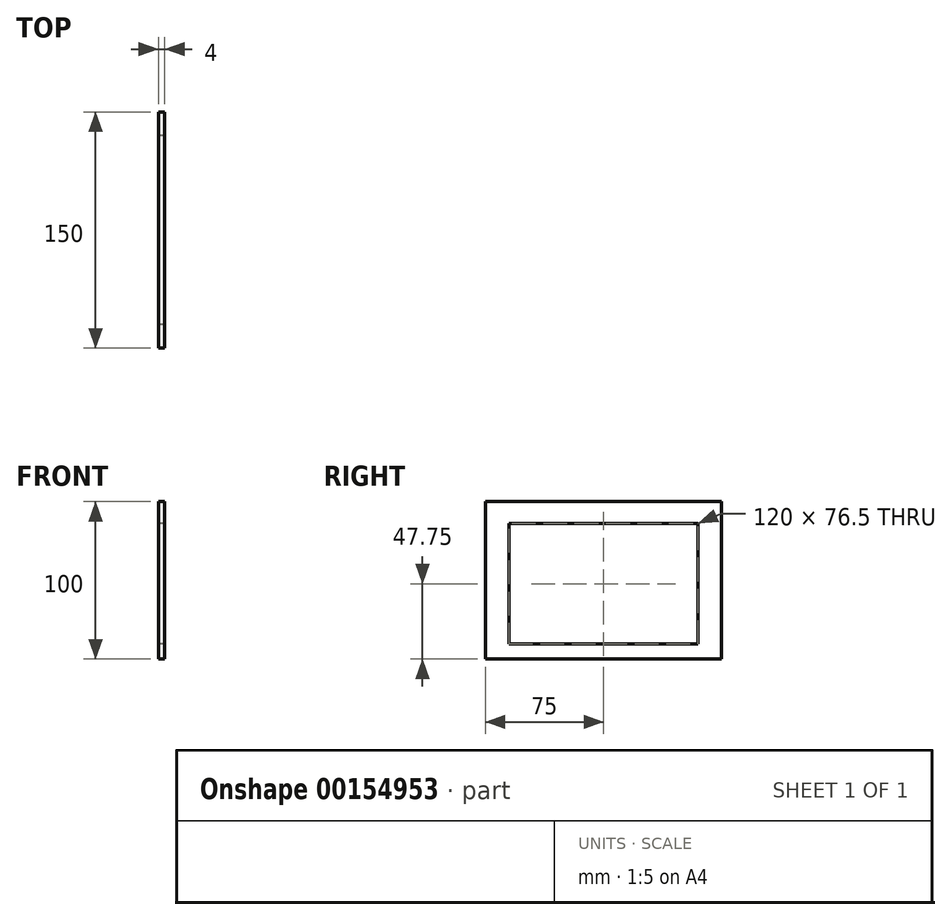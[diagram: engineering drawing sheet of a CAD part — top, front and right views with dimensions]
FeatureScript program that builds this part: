
annotation { "Feature Type Name" : "Feature", "Feature Type Description" : "" }
export const myFeature = defineFeature(function(context is Context, id is Id, definition is map)
    precondition{}
    {
        {
            var Q0;
            Q0=qCreatedBy(makeId("Right.planeOp"),FACE);
            var sketch = newSketch(context, id + "F0", { "sketchPlane" : qUnion([Q0])});
            skLineSegment(sketch, "E0.bottom", {"start": v(75, 50) * mm, "end": v(-75, 50) * mm});
            skLineSegment(sketch, "E0.top", {"start": v(75, -50) * mm, "end": v(-75, -50) * mm});
            skLineSegment(sketch, "E0.left", {"start": v(75, 50) * mm, "end": v(75, -50) * mm});
            skLineSegment(sketch, "E0.right", {"start": v(-75, 50) * mm, "end": v(-75, -50) * mm});
            skPoint(sketch, "E0.middle", {"position": v(0, 0) * mm});
            skLineSegment(sketch, "E1.bottom", {"start": v(55, 33.5) * mm, "end": v(-55, 33.5) * mm});
            skLineSegment(sketch, "E1.top", {"start": v(55, -33.5) * mm, "end": v(-55, -33.5) * mm});
            skLineSegment(sketch, "E1.left", {"start": v(55, 33.5) * mm, "end": v(55, -33.5) * mm});
            skLineSegment(sketch, "E1.right", {"start": v(-55, 33.5) * mm, "end": v(-55, -33.5) * mm});
            skLineSegment(sketch, "E2", {"start": v(0, 33.5) * mm, "end": v(0, 36) * mm});
            skPoint(sketch, "E2.endSnap0", {"position": v(0, 33.5) * mm});
            skLineSegment(sketch, "E3", {"start": v(-55, 0) * mm, "end": v(-60, 0) * mm});
            skLineSegment(sketch, "E4", {"start": v(0, -33.5) * mm, "end": v(0, -40.5) * mm});
            skPoint(sketch, "E4.endSnap0", {"position": v(0, -33.5) * mm});
            skLineSegment(sketch, "E5", {"start": v(0, -40.5) * mm, "end": v(-60, -40.5) * mm});
            skLineSegment(sketch, "E6", {"start": v(-60, 0) * mm, "end": v(-60, -40.5) * mm});
            skLineSegment(sketch, "E7", {"start": v(0, 36) * mm, "end": v(-60, 36) * mm});
            skLineSegment(sketch, "E8", {"start": v(-60, 0) * mm, "end": v(-60, 36) * mm});
            skLineSegment(sketch, "E9.MirrorCS", {"start": v(0, 36) * mm, "end": v(60, 36) * mm});
            skLineSegment(sketch, "E10.MirrorCS", {"start": v(60, 0) * mm, "end": v(60, 36) * mm});
            skLineSegment(sketch, "E11.MirrorCS", {"start": v(60, 0) * mm, "end": v(60, -40.5) * mm});
            skLineSegment(sketch, "E12.MirrorCS", {"start": v(0, -40.5) * mm, "end": v(60, -40.5) * mm});
            skSolve(sketch);
        }
        {
            var Q0;
            Q0=qSketchRegion(id+"F0",true);
            extrude(context, id + "F1", {"entities" : qUnion([Q0]), "depth" : 4 * mm});
        }
    });
